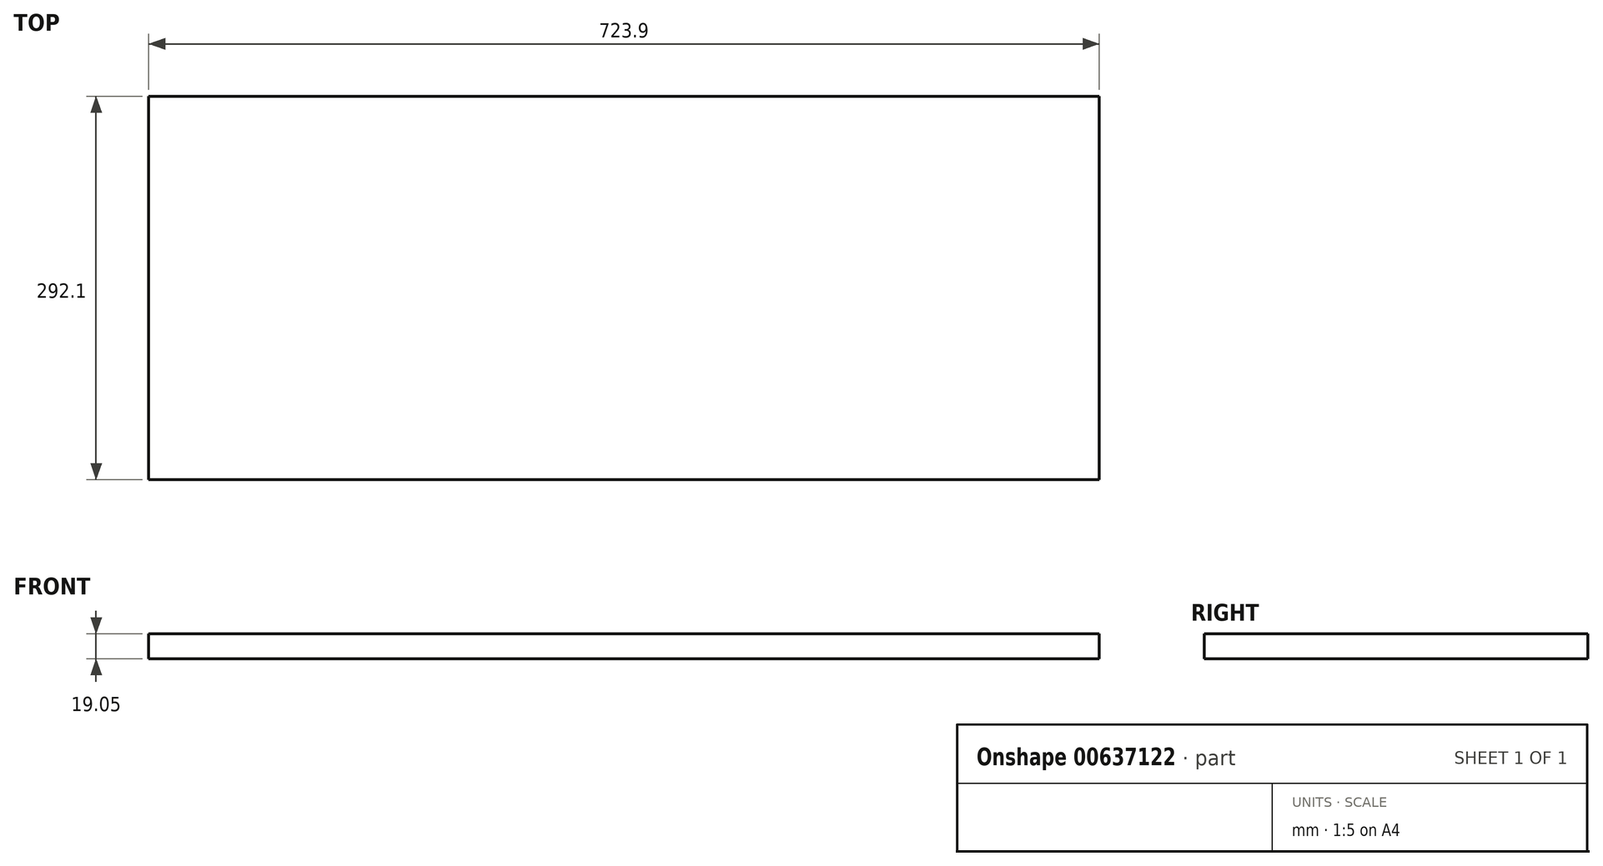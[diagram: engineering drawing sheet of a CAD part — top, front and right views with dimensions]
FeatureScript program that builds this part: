
annotation { "Feature Type Name" : "Feature", "Feature Type Description" : "" }
export const myFeature = defineFeature(function(context is Context, id is Id, definition is map)
    precondition{}
    {
        {
            var Q0;
            Q0=qCreatedBy(makeId("Top.planeOp"),FACE);
            var sketch = newSketch(context, id + "F0", { "sketchPlane" : qUnion([Q0])});
            skLineSegment(sketch, "E0.bottom", {"start": v(-361.95, 146.05) * mm, "end": v(361.95, 146.05) * mm});
            skLineSegment(sketch, "E0.top", {"start": v(-361.95, -146.05) * mm, "end": v(361.95, -146.05) * mm});
            skLineSegment(sketch, "E0.left", {"start": v(-361.95, 146.05) * mm, "end": v(-361.95, -146.05) * mm});
            skLineSegment(sketch, "E0.right", {"start": v(361.95, 146.05) * mm, "end": v(361.95, -146.05) * mm});
            skPoint(sketch, "E0.middle", {"position": v(0, 0) * mm});
            skSolve(sketch);
        }
        {
            var Q0;
            Q0=makeQuery(id+"F0.imprint","IMPRINT",FACE,{"disambiguationData":[TD([[makeQuery(id+"F0.imprint","IMPRINT",EDGE,{"derivedFrom":sQuery(id+"F0.wireOp",EDGE,"E0.bottom")}),-1.0]])]});
            extrude(context, id + "F1", {"entities" : qUnion([Q0]), "depth" : 19.05 * mm, "offsetDistance" : 25.4 * mm});
        }
    });
